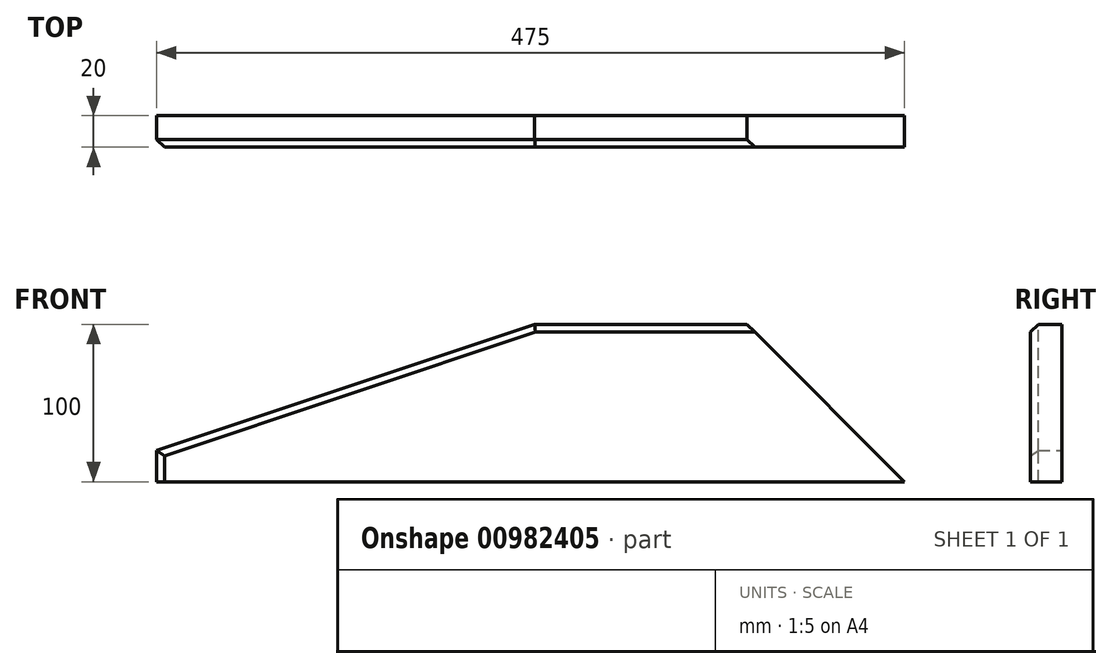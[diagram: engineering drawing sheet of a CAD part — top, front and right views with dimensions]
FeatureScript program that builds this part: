
annotation { "Feature Type Name" : "Feature", "Feature Type Description" : "" }
export const myFeature = defineFeature(function(context is Context, id is Id, definition is map)
    precondition{}
    {
        {
            var Q0;
            Q0=qCreatedBy(makeId("Front.planeOp"),FACE);
            var sketch = newSketch(context, id + "F0", { "sketchPlane" : qUnion([Q0])});
            skLineSegment(sketch, "E0.bottom", {"start": v(247.03, -18.12) * mm, "end": v(-227.97, -18.12) * mm});
            skLineSegment(sketch, "E0.top", {"start": v(247.03, 81.88) * mm, "end": v(12.03, 81.88) * mm});
            skLineSegment(sketch, "E0.left", {"start": v(247.03, -18.12) * mm, "end": v(247.03, 81.88) * mm});
            skLineSegment(sketch, "E0.right", {"start": v(-227.97, -18.12) * mm, "end": v(-227.97, 1.88) * mm});
            skPoint(sketch, "E0.middle", {"position": v(9.53, 31.88) * mm});
            skPoint(sketch, "E1", {"position": v(12.03, 81.88) * mm});
            skPoint(sketch, "E2", {"position": v(-227.97, 1.88) * mm});
            skLineSegment(sketch, "E3", {"start": v(-227.97, 1.88) * mm, "end": v(12.03, 81.88) * mm});
            skSolve(sketch);
        }
        {
            var Q0;
            Q0 = qSketchRegion(id + "F0", true);
            extrude(context, id + "F1", {"entities" : qUnion([Q0]), "depth" : 20 * mm, "offsetDistance" : 25 * mm});
        }
        {
            var Q0;
            Q0=makeQuery(id+"F1.opExtrude","CAP_EDGE",EDGE,{"disambiguationData":[OSD([sQuery(id+"F0.wireOp",EDGE,"E3")])],"isStart":false});
            var Q1;
            Q1=makeQuery(id+"F1.opExtrude","CAP_EDGE",EDGE,{"disambiguationData":[OSD([sQuery(id+"F0.wireOp",EDGE,"E0.top")])],"isStart":false});
            var Q2;
            Q2=makeQuery(id+"F1.opExtrude","CAP_EDGE",EDGE,{"disambiguationData":[OSD([sQuery(id+"F0.wireOp",EDGE,"E0.right")])],"isStart":false});
            chamfer(context, id + "F2", {"entities" : qUnion([Q0, Q1, Q2]), "width" : 5 * mm, "tangentPropagation" : true});
        }
        {
            var Q0;
            Q0=makeQuery(id+"F1.opExtrude","SWEPT_EDGE",EDGE,{"disambiguationData":[OSD([sQuery(id+"F0.wireOp",EDGE,"E0.top"),sQuery(id+"F0.wireOp",EDGE,"E0.left")])]});
            chamfer(context, id + "F3", {"entities" : qUnion([Q0]), "width" : 100 * mm, "tangentPropagation" : true});
        }
    });
